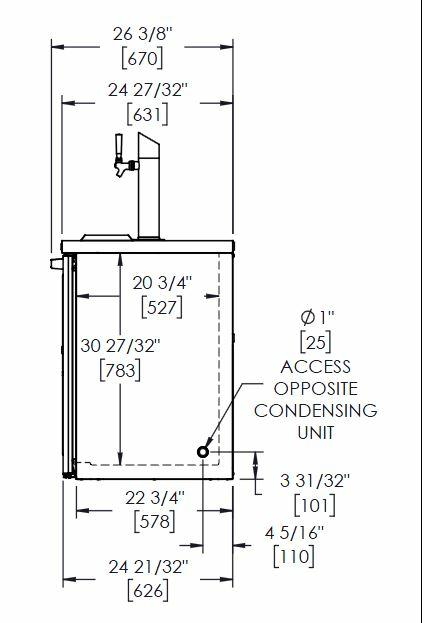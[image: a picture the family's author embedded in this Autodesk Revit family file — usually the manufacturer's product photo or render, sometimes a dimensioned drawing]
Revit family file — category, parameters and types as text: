
# Revit family: QF_TRUE_TDR48-RISZ1-L-B-SG-1
name_source: partatom
category: Specialty Equipment
revit_build: Autodesk Revit 2016 (Build: 20150714_1515(x64)
units: mm (PartAtom-declared; Revit-internal decimal feet)

## family parameters
Always vertical = Yes
Cut with Voids When Loaded = No
Part Type = Normal
Room Calculation Point = No
Round Connector Dimension = Use Diameter
Shared = No
Work Plane-Based = No

## types (1)
- QF_TRUE_TDR48-RISZ1-L-B-SG-1
    Apparent Power = 207 VA
    Condensate Return Connection Height = 0"
    Condensate Return RI Height = 0"
    Condensate Return Size = 1"
    Conn Conduit = Yes
    Conn Plug = NEMA 5-15P
    Cycle = 60 Hz
    Depth = 26 3/8"
    Description = REACH-IN SINGLE ZONE REFRIGERATOR WITH LEFT SIDE REFRIGERATION SYSTEM. BLACK EXTERIOR AND SOLID & GLASS SWING DOORS
    Elec Conn Connection Height = 0"
    Elec Conn RI Height = 0"
    FL Amps = 2 A
    Foodservice Equipment Identifier = Yes
    HP = 1/4
    Identify Quantity as Lot = Yes
    Indirect Waste Connection Height = 0"
    Indirect Waste Flow = 0 GPM
    Indirect Waste Size = 1"
    Length = 48"
    Manufacturer = TRUE
    Max Overcurrent Protection = 0 A
    Min Ckt Ampacity = 0 A
    Model = TDR48-RISZ1-L-B-SG-1
    Number of Poles = 1
    Phase = 1
    Steam Supply Connection Height = 0"
    Steam Supply Maximum Pressure = 0.00 psi
    Steam Supply Minimum Pressure = 0.00 psi
    Steam Supply RI Height = 0"
    Steam Supply Size = 0"
    Steam Supply Volume = 0 GPM
    Volts = 115 V
    Waste Water Discharge Temperature = 0 °F
    Watts = 207 W
    Weight in Pounds = 405

## geometry (parser evidence)
native form markers: Sweep x22
no freeform markers — native parametric forms only
